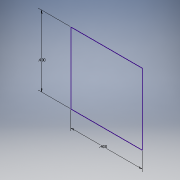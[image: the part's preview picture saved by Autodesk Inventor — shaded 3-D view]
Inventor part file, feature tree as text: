
AUTODESK INVENTOR PART (.ipt)
format: ipt  version: 2018 (Build 220112000, 112)  size: 91,136 bytes
history: native  units: in
note: dims shown in document units (in); Inventor stores cm internally (conversion verified against a paired STEP export)
features: sketch x1
ambient origin geometry x8: Origin, YZ Plane, XZ Plane, XY Plane, X Axis, Y Axis, Z Axis, Center Point
feature tree (1):
  sketch  "Sketch1"  dims[d24=0.105in d25=0.21in d34=0.0in d35=0.25in d39=0.4in d40=0.4in]
